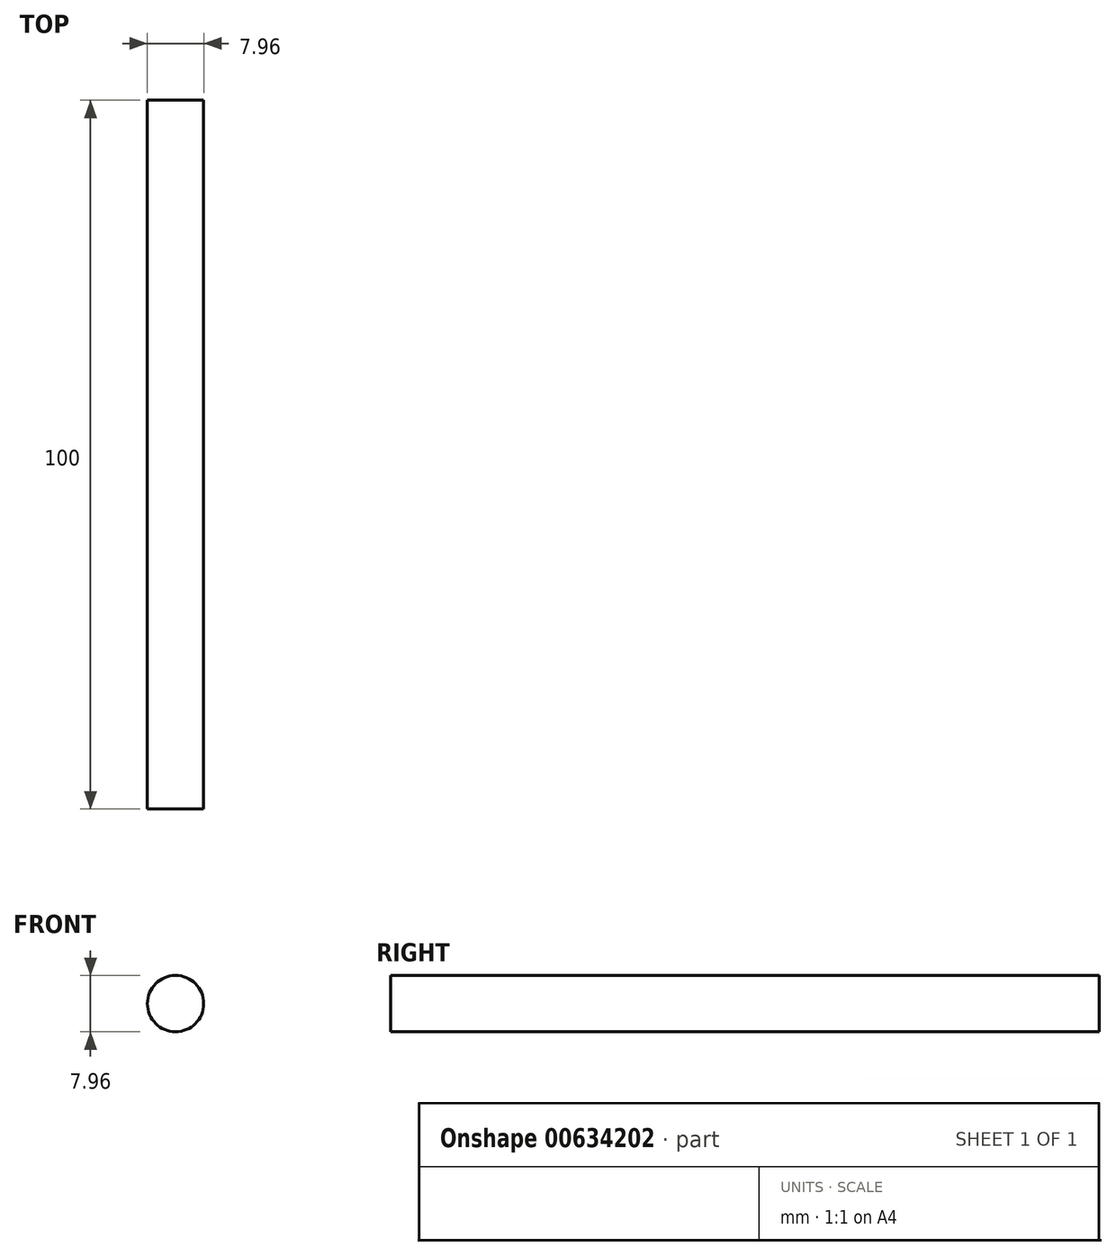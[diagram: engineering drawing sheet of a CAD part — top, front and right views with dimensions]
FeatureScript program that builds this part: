
annotation { "Feature Type Name" : "Feature", "Feature Type Description" : "" }
export const myFeature = defineFeature(function(context is Context, id is Id, definition is map)
    precondition{}
    {
        {
            var Q0;
            Q0=qCreatedBy(makeId("Front.planeOp"),FACE);
            var sketch = newSketch(context, id + "F0", { "sketchPlane" : qUnion([Q0])});
            skCircle(sketch, "E0", {"center": v(0, 0) * mm, "radius": 3.98 * mm});
            skSolve(sketch);
        }
        {
            var Q0;
            Q0=makeQuery(id+"F0.imprint","IMPRINT",FACE,{"disambiguationData":[TD([[makeQuery(id+"F0.imprint","IMPRINT",EDGE,{"derivedFrom":sQuery(id+"F0.wireOp",EDGE,"E0")}),1.0]])]});
            extrude(context, id + "F1", {"entities" : qUnion([Q0]), "depth" : 100 * mm, "offsetDistance" : 25 * mm});
        }
    });
